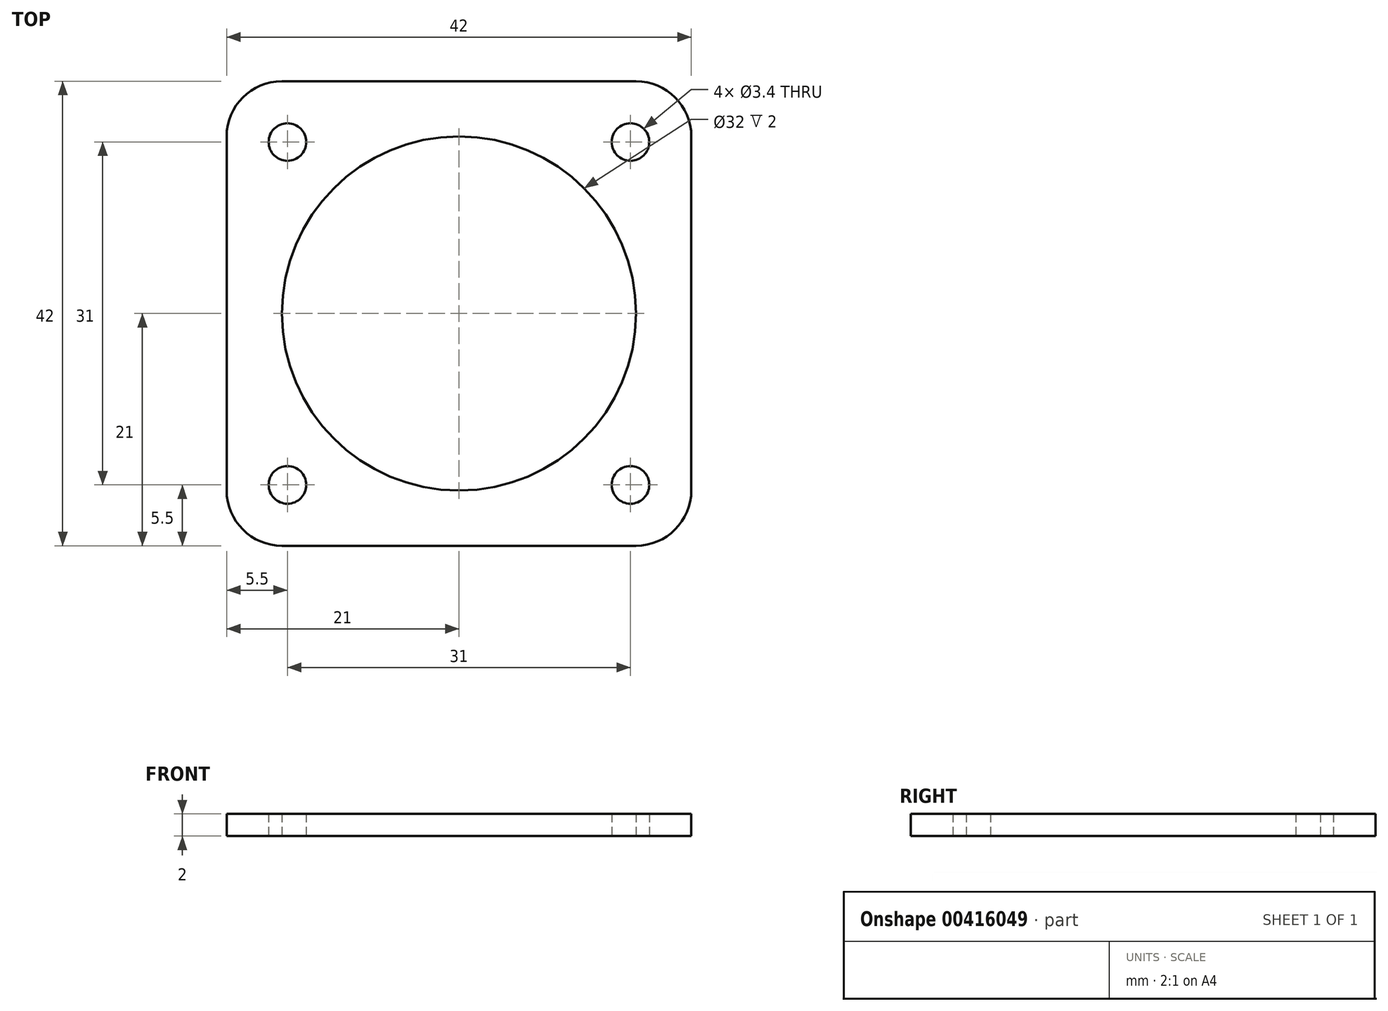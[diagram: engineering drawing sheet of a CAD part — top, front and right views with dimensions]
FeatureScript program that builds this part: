
annotation { "Feature Type Name" : "Feature", "Feature Type Description" : "" }
export const myFeature = defineFeature(function(context is Context, id is Id, definition is map)
    precondition{}
    {
        {
            var Q0;
            Q0=qCreatedBy(makeId("Top.planeOp"),FACE);
            var sketch = newSketch(context, id + "F0", { "sketchPlane" : qUnion([Q0])});
            skLineSegment(sketch, "E0.bottom", {"start": v(21, -21) * mm, "end": v(-21, -21) * mm});
            skLineSegment(sketch, "E0.top", {"start": v(21, 21) * mm, "end": v(-21, 21) * mm});
            skLineSegment(sketch, "E0.left", {"start": v(21, -21) * mm, "end": v(21, 21) * mm});
            skLineSegment(sketch, "E0.right", {"start": v(-21, -21) * mm, "end": v(-21, 21) * mm});
            skPoint(sketch, "E0.middle", {"position": v(0, 0) * mm});
            skCircle(sketch, "E1", {"center": v(-15.5, 15.5) * mm, "radius": 1.7 * mm});
            skCircle(sketch, "E2.MirrorC", {"center": v(15.5, 15.5) * mm, "radius": 1.7 * mm});
            skCircle(sketch, "E3.MirrorC", {"center": v(-15.5, -15.5) * mm, "radius": 1.7 * mm});
            skCircle(sketch, "E4.MirrorC", {"center": v(15.5, -15.5) * mm, "radius": 1.7 * mm});
            skCircle(sketch, "E5", {"center": v(0, 0) * mm, "radius": 16 * mm});
            skSolve(sketch);
        }
        {
            var Q0;
            Q0 = qSketchRegion(id + "F0", true);
            extrude(context, id + "F1", {"entities" : qUnion([Q0]), "depth" : 2 * mm, "offsetDistance" : 25 * mm});
        }
        {
            var Q0;
            Q0=makeQuery(id+"F1.opExtrude","SWEPT_EDGE",EDGE,{"disambiguationData":[OSD([sQuery(id+"F0.wireOp",EDGE,"E0.bottom"),sQuery(id+"F0.wireOp",EDGE,"E0.right")])]});
            var Q1;
            Q1=makeQuery(id+"F1.opExtrude","SWEPT_EDGE",EDGE,{"disambiguationData":[OSD([sQuery(id+"F0.wireOp",EDGE,"E0.bottom"),sQuery(id+"F0.wireOp",EDGE,"E0.left")])]});
            var Q2;
            Q2=makeQuery(id+"F1.opExtrude","SWEPT_EDGE",EDGE,{"disambiguationData":[OSD([sQuery(id+"F0.wireOp",EDGE,"E0.top"),sQuery(id+"F0.wireOp",EDGE,"E0.right")])]});
            var Q3;
            Q3=makeQuery(id+"F1.opExtrude","SWEPT_EDGE",EDGE,{"disambiguationData":[OSD([sQuery(id+"F0.wireOp",EDGE,"E0.top"),sQuery(id+"F0.wireOp",EDGE,"E0.left")])]});
            fillet(context, id + "F2", {"entities" : qUnion([Q0, Q1, Q2, Q3]), "tangentPropagation" : true, "radius" : 5 * mm, "defaultsChanged" : false, "vertexSettings" : [], "allowEdgeOverflow" : false});
        }
    });
